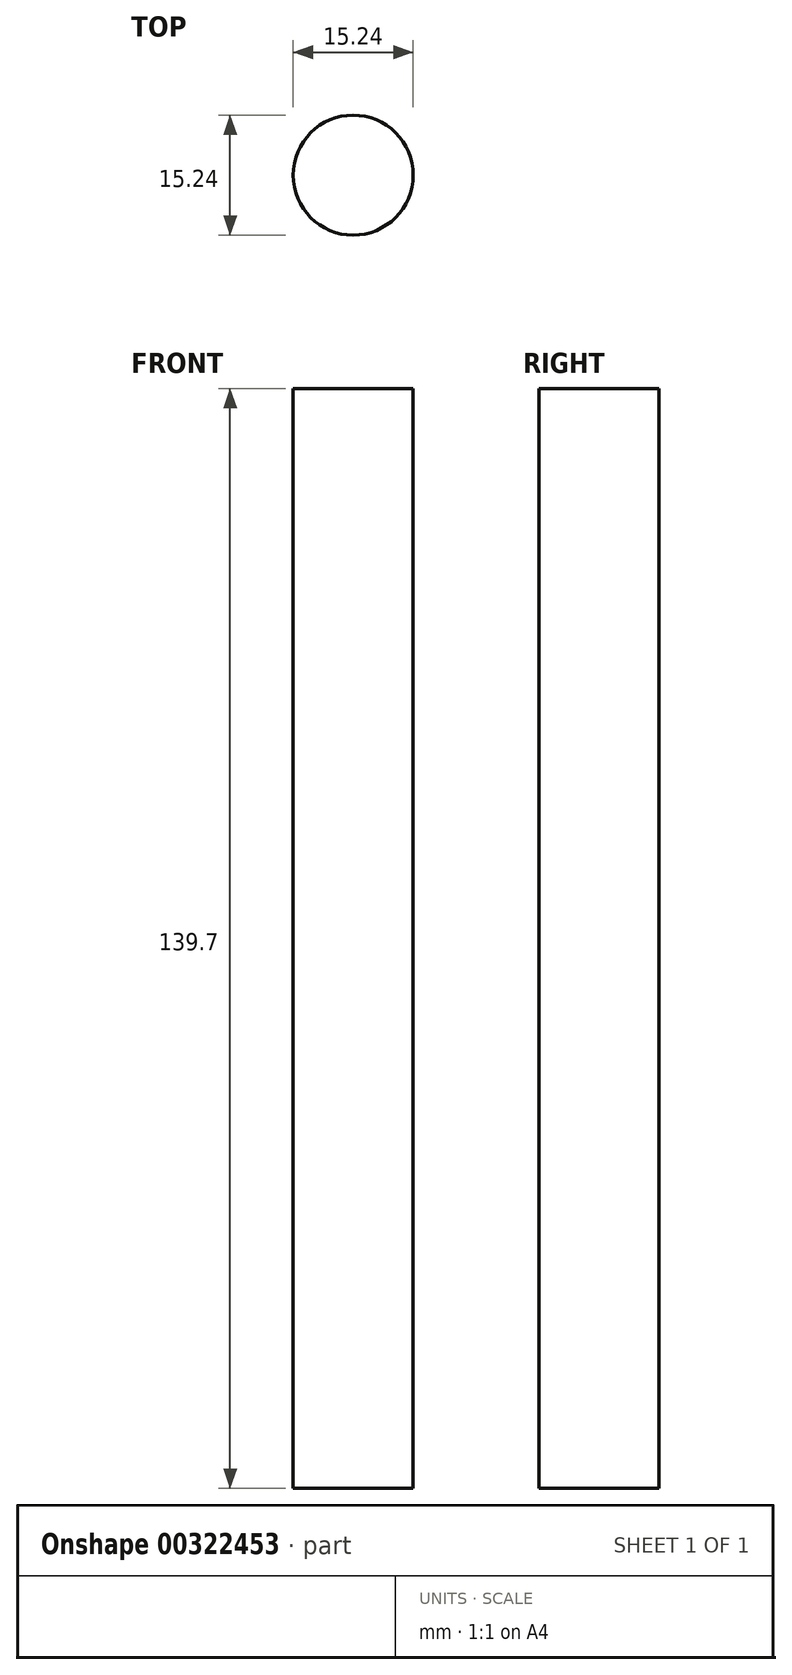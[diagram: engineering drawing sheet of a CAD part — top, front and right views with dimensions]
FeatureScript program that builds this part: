
annotation { "Feature Type Name" : "Feature", "Feature Type Description" : "" }
export const myFeature = defineFeature(function(context is Context, id is Id, definition is map)
    precondition{}
    {
        {
            var Q0;
            Q0=qCreatedBy(makeId("Top.planeOp"),FACE);
            var sketch = newSketch(context, id + "F0", { "sketchPlane" : qUnion([Q0])});
            skCircle(sketch, "E0", {"center": v(0, 0) * mm, "radius": 7.62 * mm});
            skSolve(sketch);
        }
        {
            var Q0;
            Q0 = qSketchRegion(id + "F0", true);
            extrude(context, id + "F1", {"entities" : qUnion([Q0]), "depth" : 139.7 * mm});
        }
    });
